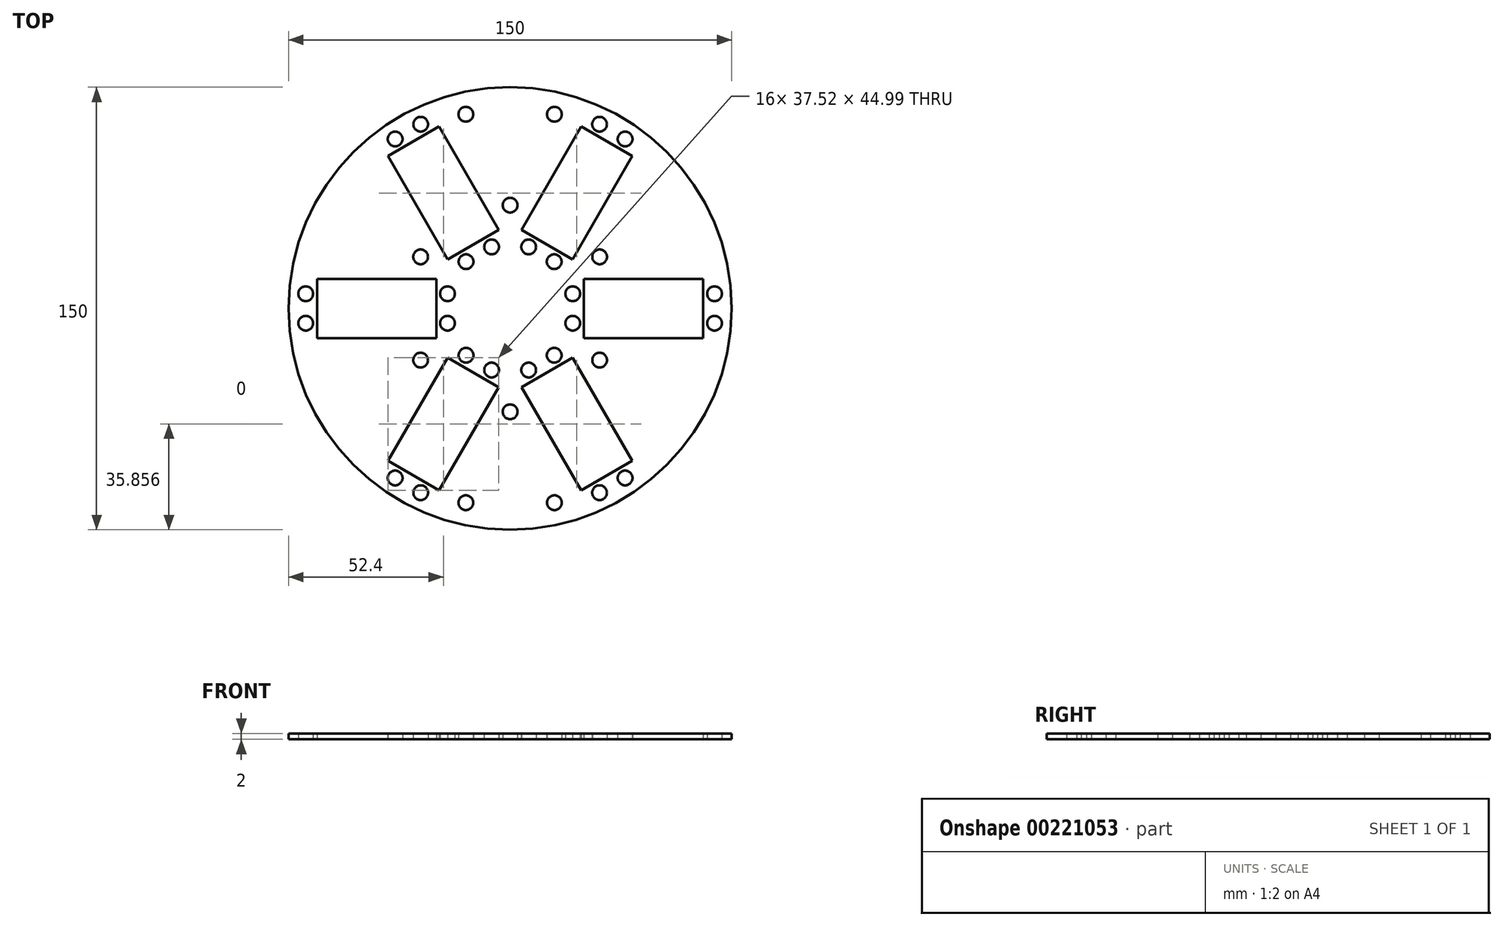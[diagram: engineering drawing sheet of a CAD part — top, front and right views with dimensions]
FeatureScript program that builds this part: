
annotation { "Feature Type Name" : "Feature", "Feature Type Description" : "" }
export const myFeature = defineFeature(function(context is Context, id is Id, definition is map)
    precondition{}
    {
        {
            var Q0;
            Q0=qCreatedBy(makeId("Top.planeOp"),FACE);
            var sketch = newSketch(context, id + "F0", { "sketchPlane" : qUnion([Q0])});
            skCircle(sketch, "E0", {"center": v(0, 0) * mm, "radius": 75 * mm});
            skLineSegment(sketch, "E1.bottom", {"start": v(-65.4, 10) * mm, "end": v(-25, 10) * mm});
            skLineSegment(sketch, "E1.top", {"start": v(-65.4, -10) * mm, "end": v(-25, -10) * mm});
            skLineSegment(sketch, "E1.left", {"start": v(-65.4, 10) * mm, "end": v(-65.4, -10) * mm});
            skLineSegment(sketch, "E1.right", {"start": v(-25, 10) * mm, "end": v(-25, -10) * mm});
            skLineSegment(sketch, "E2.1.0", {"start": v(-21.16, -16.65) * mm, "end": v(-3.84, -26.65) * mm});
            skLineSegment(sketch, "E2.1.1", {"start": v(-41.36, -51.64) * mm, "end": v(-21.16, -16.65) * mm});
            skLineSegment(sketch, "E2.1.2", {"start": v(-41.36, -51.64) * mm, "end": v(-24.04, -61.64) * mm});
            skLineSegment(sketch, "E2.1.3", {"start": v(-24.04, -61.64) * mm, "end": v(-3.84, -26.65) * mm});
            skLineSegment(sketch, "E2.2.0", {"start": v(3.84, -26.65) * mm, "end": v(21.16, -16.65) * mm});
            skLineSegment(sketch, "E2.2.1", {"start": v(24.04, -61.64) * mm, "end": v(3.84, -26.65) * mm});
            skLineSegment(sketch, "E2.2.2", {"start": v(24.04, -61.64) * mm, "end": v(41.36, -51.64) * mm});
            skLineSegment(sketch, "E2.2.3", {"start": v(41.36, -51.64) * mm, "end": v(21.16, -16.65) * mm});
            skLineSegment(sketch, "E2.3.0", {"start": v(25, -10) * mm, "end": v(25, 10) * mm});
            skLineSegment(sketch, "E2.3.1", {"start": v(65.4, -10) * mm, "end": v(25, -10) * mm});
            skLineSegment(sketch, "E2.3.2", {"start": v(65.4, -10) * mm, "end": v(65.4, 10) * mm});
            skLineSegment(sketch, "E2.3.3", {"start": v(65.4, 10) * mm, "end": v(25, 10) * mm});
            skLineSegment(sketch, "E2.4.0", {"start": v(21.16, 16.65) * mm, "end": v(3.84, 26.65) * mm});
            skLineSegment(sketch, "E2.4.1", {"start": v(41.36, 51.64) * mm, "end": v(21.16, 16.65) * mm});
            skLineSegment(sketch, "E2.4.2", {"start": v(41.36, 51.64) * mm, "end": v(24.04, 61.64) * mm});
            skLineSegment(sketch, "E2.4.3", {"start": v(24.04, 61.64) * mm, "end": v(3.84, 26.65) * mm});
            skLineSegment(sketch, "E2.5.0", {"start": v(-3.84, 26.65) * mm, "end": v(-21.16, 16.65) * mm});
            skLineSegment(sketch, "E2.5.1", {"start": v(-24.04, 61.64) * mm, "end": v(-3.84, 26.65) * mm});
            skLineSegment(sketch, "E2.5.2", {"start": v(-24.04, 61.64) * mm, "end": v(-41.36, 51.64) * mm});
            skLineSegment(sketch, "E2.5.3", {"start": v(-41.36, 51.64) * mm, "end": v(-21.16, 16.65) * mm});
            skCircle(sketch, "E3", {"center": v(15, 65.81) * mm, "radius": 2.5 * mm});
            skCircle(sketch, "E4.1.0", {"center": v(-15, -65.81) * mm, "radius": 2.5 * mm});
            skLineSegment(sketch, "E4.anchor1", {"start": v(0, 0) * mm, "end": v(15, 65.81) * mm, "construction": true});
            skLineSegment(sketch, "E4.anchor2", {"start": v(0, 0) * mm, "end": v(-15, -65.81) * mm, "construction": true});
            skCircle(sketch, "E5.MirrorC", {"center": v(15, -65.81) * mm, "radius": 2.5 * mm});
            skCircle(sketch, "E6.MirrorC", {"center": v(-15, 65.81) * mm, "radius": 2.5 * mm});
            skCircle(sketch, "E7", {"center": v(-69.2, 5) * mm, "radius": 2.5 * mm});
            skCircle(sketch, "E8.MirrorC", {"center": v(-69.2, -5) * mm, "radius": 2.5 * mm});
            skCircle(sketch, "E9", {"center": v(-21.2, 5) * mm, "radius": 2.5 * mm});
            skCircle(sketch, "E10.MirrorC", {"center": v(-21.2, -5) * mm, "radius": 2.5 * mm});
            skCircle(sketch, "E11.1.0", {"center": v(-14.93, -15.86) * mm, "radius": 2.5 * mm});
            skCircle(sketch, "E11.1.1", {"center": v(-6.27, -20.86) * mm, "radius": 2.5 * mm});
            skCircle(sketch, "E11.1.2", {"center": v(-38.93, -57.43) * mm, "radius": 2.5 * mm});
            skCircle(sketch, "E11.1.3", {"center": v(-30.27, -62.43) * mm, "radius": 2.5 * mm});
            skCircle(sketch, "E11.2.0", {"center": v(6.27, -20.86) * mm, "radius": 2.5 * mm});
            skCircle(sketch, "E11.2.1", {"center": v(14.93, -15.86) * mm, "radius": 2.5 * mm});
            skCircle(sketch, "E11.2.2", {"center": v(30.27, -62.43) * mm, "radius": 2.5 * mm});
            skCircle(sketch, "E11.2.3", {"center": v(38.93, -57.43) * mm, "radius": 2.5 * mm});
            skCircle(sketch, "E11.3.0", {"center": v(21.2, -5) * mm, "radius": 2.5 * mm});
            skCircle(sketch, "E11.3.1", {"center": v(21.2, 5) * mm, "radius": 2.5 * mm});
            skCircle(sketch, "E11.3.2", {"center": v(69.2, -5) * mm, "radius": 2.5 * mm});
            skCircle(sketch, "E11.3.3", {"center": v(69.2, 5) * mm, "radius": 2.5 * mm});
            skCircle(sketch, "E11.4.0", {"center": v(14.93, 15.86) * mm, "radius": 2.5 * mm});
            skCircle(sketch, "E11.4.1", {"center": v(6.27, 20.86) * mm, "radius": 2.5 * mm});
            skCircle(sketch, "E11.4.2", {"center": v(38.93, 57.43) * mm, "radius": 2.5 * mm});
            skCircle(sketch, "E11.4.3", {"center": v(30.27, 62.43) * mm, "radius": 2.5 * mm});
            skCircle(sketch, "E11.5.0", {"center": v(-6.27, 20.86) * mm, "radius": 2.5 * mm});
            skCircle(sketch, "E11.5.1", {"center": v(-14.93, 15.86) * mm, "radius": 2.5 * mm});
            skCircle(sketch, "E11.5.2", {"center": v(-30.27, 62.43) * mm, "radius": 2.5 * mm});
            skCircle(sketch, "E11.5.3", {"center": v(-38.93, 57.43) * mm, "radius": 2.5 * mm});
            skCircle(sketch, "E12", {"center": v(0, 35) * mm, "radius": 2.5 * mm});
            skCircle(sketch, "E13.1.0", {"center": v(-30.31, 17.5) * mm, "radius": 2.5 * mm});
            skCircle(sketch, "E13.2.0", {"center": v(-30.31, -17.5) * mm, "radius": 2.5 * mm});
            skCircle(sketch, "E13.3.0", {"center": v(0, -35) * mm, "radius": 2.5 * mm});
            skCircle(sketch, "E13.4.0", {"center": v(30.31, -17.5) * mm, "radius": 2.5 * mm});
            skCircle(sketch, "E13.5.0", {"center": v(30.31, 17.5) * mm, "radius": 2.5 * mm});
            skSolve(sketch);
        }
        {
            var Q0;
            Q0=makeQuery(id+"F0.imprint","IMPRINT",FACE,{"disambiguationData":[TD([[makeQuery(id+"F0.imprint","IMPRINT",EDGE,{"derivedFrom":sQuery(id+"F0.wireOp",EDGE,"E0")}),1.0]])]});
            extrude(context, id + "F1", {"entities" : qUnion([Q0]), "depth" : 2 * mm});
        }
    });
